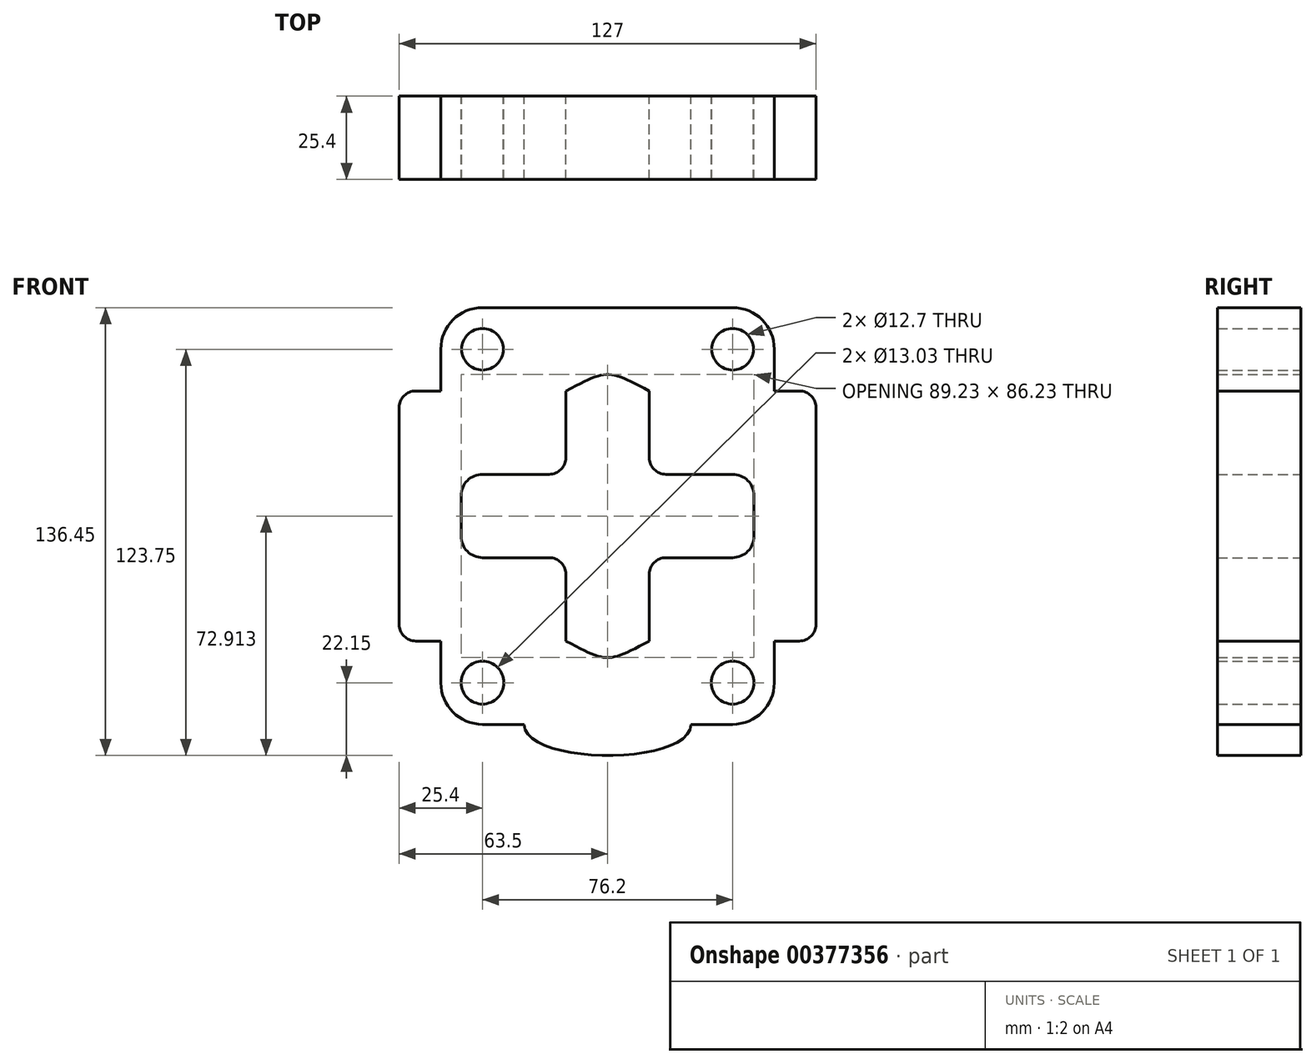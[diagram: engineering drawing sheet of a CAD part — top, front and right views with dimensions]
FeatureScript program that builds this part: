
annotation { "Feature Type Name" : "Feature", "Feature Type Description" : "" }
export const myFeature = defineFeature(function(context is Context, id is Id, definition is map)
    precondition{}
    {
        {
            var Q0;
            Q0=qCreatedBy(makeId("Front.planeOp"),FACE);
            var sketch = newSketch(context, id + "F0", { "sketchPlane" : qUnion([Q0])});
            skLineSegment(sketch, "E0", {"start": v(-50.8, 63.5) * mm, "end": v(0, 63.5) * mm});
            skLineSegment(sketch, "E1", {"start": v(0, 63.5) * mm, "end": v(50.8, 63.5) * mm});
            skLineSegment(sketch, "E2", {"start": v(-50.8, 63.5) * mm, "end": v(-50.8, 38.1) * mm});
            skLineSegment(sketch, "E3", {"start": v(50.8, 63.5) * mm, "end": v(50.8, 38.1) * mm});
            skLineSegment(sketch, "E4", {"start": v(50.8, 38.1) * mm, "end": v(63.5, 38.1) * mm});
            skLineSegment(sketch, "E5", {"start": v(-50.8, 38.1) * mm, "end": v(-63.5, 38.1) * mm});
            skLineSegment(sketch, "E6", {"start": v(-63.5, 38.1) * mm, "end": v(-63.5, -38.1) * mm});
            skLineSegment(sketch, "E7", {"start": v(63.5, 38.1) * mm, "end": v(63.5, -38.1) * mm});
            skLineSegment(sketch, "E8", {"start": v(63.5, -38.1) * mm, "end": v(50.8, -38.1) * mm});
            skLineSegment(sketch, "E9", {"start": v(-63.5, -38.1) * mm, "end": v(-50.8, -38.1) * mm});
            skLineSegment(sketch, "E10", {"start": v(-50.8, -38.1) * mm, "end": v(-50.8, -63.5) * mm});
            skLineSegment(sketch, "E11", {"start": v(50.8, -38.1) * mm, "end": v(50.8, -63.5) * mm});
            skLineSegment(sketch, "E12", {"start": v(-50.8, -63.5) * mm, "end": v(-25.4, -63.5) * mm});
            skLineSegment(sketch, "E13", {"start": v(50.8, -63.5) * mm, "end": v(25.4, -63.5) * mm});
            skFitSpline(sketch, "E14", {"points": [v(-25.4, -63.5) * mm, v(25.4, -63.5) * mm], "startDerivative": vector(0.8, -37.39) * mm, "endDerivative": vector(0.8, 38.24) * mm});
            skLineSegment(sketch, "E15", {"start": v(-12.7, 38.1) * mm, "end": v(-12.7, 12.7) * mm});
            skLineSegment(sketch, "E16", {"start": v(-12.7, 12.7) * mm, "end": v(-38.1, 12.7) * mm});
            skLineSegment(sketch, "E17", {"start": v(12.7, 38.1) * mm, "end": v(12.7, 12.7) * mm});
            skLineSegment(sketch, "E18", {"start": v(12.7, 12.7) * mm, "end": v(38.1, 12.7) * mm});
            skLineSegment(sketch, "E19", {"start": v(12.7, -12.7) * mm, "end": v(38.1, -12.7) * mm});
            skLineSegment(sketch, "E20", {"start": v(-12.7, -12.7) * mm, "end": v(-38.1, -12.7) * mm});
            skLineSegment(sketch, "E21", {"start": v(-12.7, -12.7) * mm, "end": v(-12.7, -38.1) * mm});
            skLineSegment(sketch, "E22", {"start": v(12.7, -12.7) * mm, "end": v(12.7, -38.1) * mm});
            skArc(sketch, "E23", {"start": v(-38.1, 12.7) * mm, "mid": v(-42.7, 10.8) * mm, "end": v(-44.62, 6.18) * mm});
            skArc(sketch, "E24", {"start": v(-38.1, -12.7) * mm, "mid": v(-42.7, -10.8) * mm, "end": v(-44.62, -6.18) * mm});
            skArc(sketch, "E25", {"start": v(38.1, 12.7) * mm, "mid": v(42.7, 10.8) * mm, "end": v(44.62, 6.18) * mm});
            skArc(sketch, "E26", {"start": v(38.1, -12.7) * mm, "mid": v(42.7, -10.8) * mm, "end": v(44.62, -6.18) * mm});
            skLineSegment(sketch, "E27", {"start": v(-44.62, 6.18) * mm, "end": v(-44.62, -6.18) * mm});
            skLineSegment(sketch, "E28", {"start": v(44.62, 6.18) * mm, "end": v(44.62, -6.18) * mm});
            skFitSpline(sketch, "E29", {"points": [v(-12.7, 38.1) * mm, v(12.7, 38.1) * mm], "startDerivative": vector(38.1, 19.92) * mm, "endDerivative": vector(38.1, -19.92) * mm});
            skFitSpline(sketch, "E30", {"points": [v(12.7, -38.1) * mm, v(-12.7, -38.1) * mm], "startDerivative": vector(-38.1, -20.2) * mm, "endDerivative": vector(-38.1, 20.2) * mm});
            skArc(sketch, "E31", {"start": v(-38.1, 63.5) * mm, "mid": v(-47.08, 59.78) * mm, "end": v(-50.8, 50.8) * mm});
            skArc(sketch, "E32", {"start": v(50.8, 50.8) * mm, "mid": v(47.08, 59.78) * mm, "end": v(38.1, 63.5) * mm});
            skArc(sketch, "E33", {"start": v(-50.8, -50.8) * mm, "mid": v(-47.08, -59.78) * mm, "end": v(-38.1, -63.5) * mm});
            skArc(sketch, "E34", {"start": v(38.1, -63.5) * mm, "mid": v(47.08, -59.78) * mm, "end": v(50.8, -50.8) * mm});
            skCircle(sketch, "E35", {"center": v(-38.1, 50.8) * mm, "radius": 6.35 * mm});
            skCircle(sketch, "E36", {"center": v(38.1, 50.8) * mm, "radius": 6.35 * mm});
            skCircle(sketch, "E37", {"center": v(-38.1, -50.8) * mm, "radius": 6.52 * mm});
            skCircle(sketch, "E38", {"center": v(38.1, -50.8) * mm, "radius": 6.52 * mm});
            skSolve(sketch);
        }
        {
            var Q0;
            {var subQ12=sQuery(id+"F0.wireOp",EDGE,"E4");Q0=makeQuery(id+"F0.imprint","IMPRINT",FACE,{"disambiguationData":[TD([[makeQuery(id+"F0.imprint","IMPRINT",EDGE,{"derivedFrom":subQ12}),-1.0]])]});}
            extrude(context, id + "F1", {"entities" : qUnion([Q0]), "endBound" : BoundingType.SYMMETRIC, "depth" : 25.4 * mm});
        }
        {
            var Q0;
            Q0=makeQuery(id+"F1.opExtrude","SWEPT_EDGE",EDGE,{"disambiguationData":[OSD([sQuery(id+"F0.wireOp",EDGE,"E17"),sQuery(id+"F0.wireOp",EDGE,"E18")])]});
            var Q1;
            Q1=makeQuery(id+"F1.opExtrude","SWEPT_EDGE",EDGE,{"disambiguationData":[OSD([sQuery(id+"F0.wireOp",EDGE,"E15"),sQuery(id+"F0.wireOp",EDGE,"E16")])]});
            var Q2;
            Q2=makeQuery(id+"F1.opExtrude","SWEPT_EDGE",EDGE,{"disambiguationData":[OSD([sQuery(id+"F0.wireOp",EDGE,"E19"),sQuery(id+"F0.wireOp",EDGE,"E22")])]});
            var Q3;
            Q3=makeQuery(id+"F1.opExtrude","SWEPT_EDGE",EDGE,{"disambiguationData":[OSD([sQuery(id+"F0.wireOp",EDGE,"E20"),sQuery(id+"F0.wireOp",EDGE,"E21")])]});
            var Q4;
            Q4=makeQuery(id+"F1.opExtrude","SWEPT_EDGE",EDGE,{"disambiguationData":[OSD([sQuery(id+"F0.wireOp",EDGE,"E5"),sQuery(id+"F0.wireOp",EDGE,"E6")])]});
            var Q5;
            Q5=makeQuery(id+"F1.opExtrude","SWEPT_EDGE",EDGE,{"disambiguationData":[OSD([sQuery(id+"F0.wireOp",EDGE,"E6"),sQuery(id+"F0.wireOp",EDGE,"E9")])]});
            var Q6;
            Q6=makeQuery(id+"F1.opExtrude","SWEPT_EDGE",EDGE,{"disambiguationData":[OSD([sQuery(id+"F0.wireOp",EDGE,"E7"),sQuery(id+"F0.wireOp",EDGE,"E8")])]});
            var Q7;
            Q7=makeQuery(id+"F1.opExtrude","SWEPT_EDGE",EDGE,{"disambiguationData":[OSD([sQuery(id+"F0.wireOp",EDGE,"E4"),sQuery(id+"F0.wireOp",EDGE,"E7")])]});
            fillet(context, id + "F2", {"entities" : qUnion([Q0, Q1, Q2, Q3, Q4, Q5, Q6, Q7]), "radius" : 5.08 * mm, "tangentPropagation" : true, "allowEdgeOverflow" : false});
        }
    });
